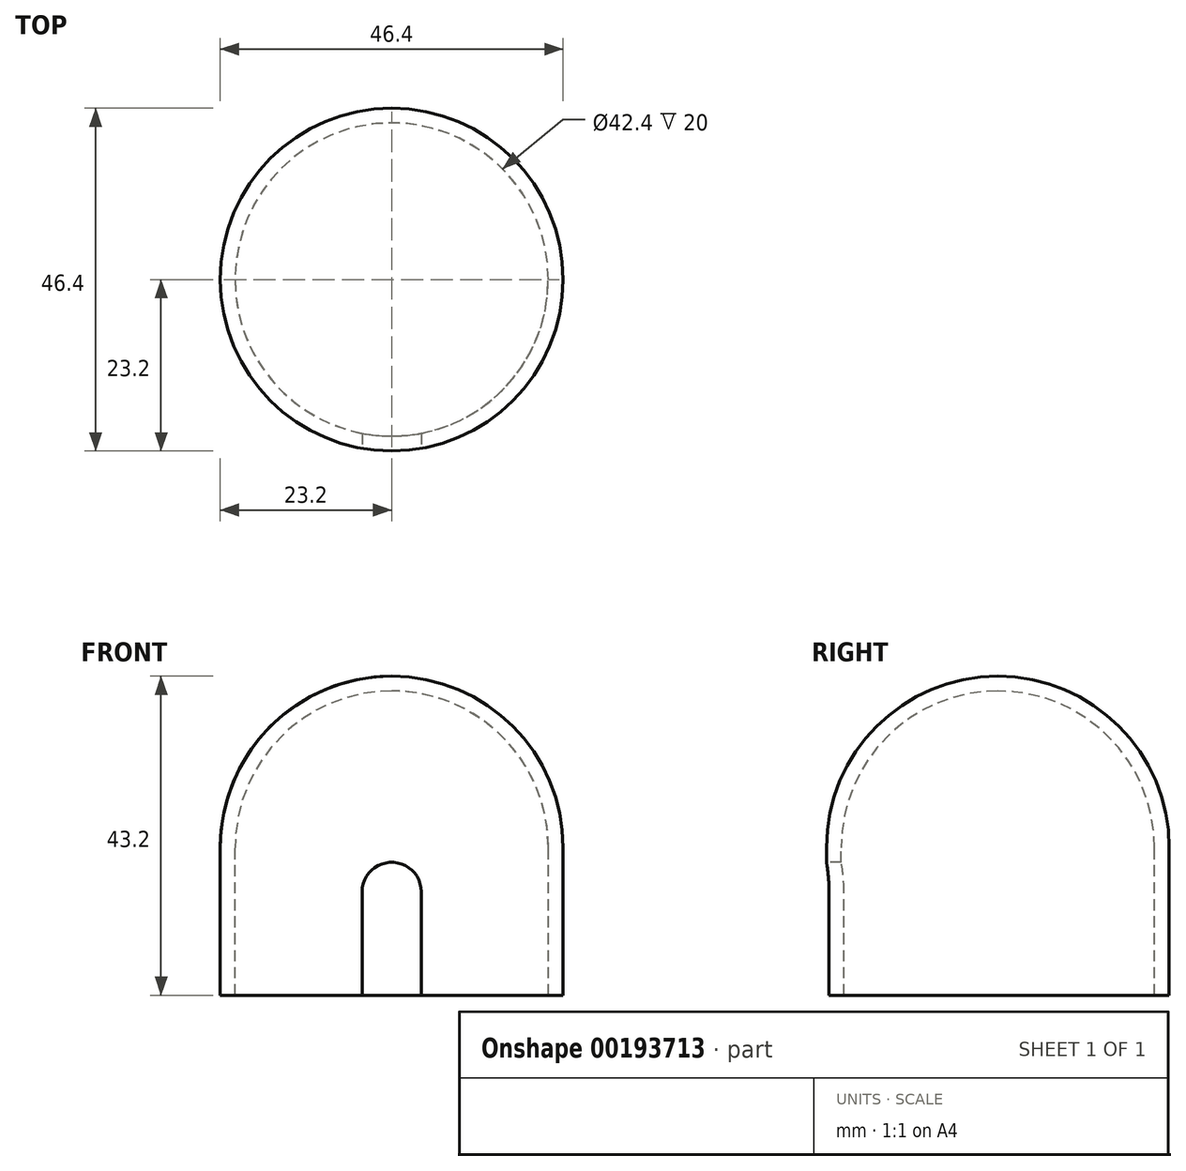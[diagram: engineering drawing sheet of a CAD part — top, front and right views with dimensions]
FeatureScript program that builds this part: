
annotation { "Feature Type Name" : "Feature", "Feature Type Description" : "" }
export const myFeature = defineFeature(function(context is Context, id is Id, definition is map)
    precondition{}
    {
        {
            var Q0;
            Q0=qCreatedBy(makeId("Front.planeOp"),FACE);
            var sketch = newSketch(context, id + "F0", { "sketchPlane" : qUnion([Q0])});
            skLineSegment(sketch, "E0", {"start": v(-21.2, 0) * mm, "end": v(-21.2, 20) * mm});
            skArc(sketch, "E1", {"start": v(-21.2, 20) * mm, "mid": v(-15, 35) * mm, "end": v(0, 41.2) * mm});
            skArc(sketch, "E2.0", {"start": v(-23.2, 20) * mm, "mid": v(-16.4, 36.4) * mm, "end": v(0, 43.2) * mm});
            skLineSegment(sketch, "E2.1", {"start": v(-23.2, 0) * mm, "end": v(-23.2, 20) * mm});
            skLineSegment(sketch, "E3", {"start": v(-23.2, 0) * mm, "end": v(-21.2, 0) * mm});
            skLineSegment(sketch, "E4", {"start": v(0, 41.2) * mm, "end": v(0, 43.2) * mm});
            skSolve(sketch);
        }
        {
            var Q0;
            Q0=qCreatedBy(makeId("Front.planeOp"),FACE);
            var sketch = newSketch(context, id + "F1", { "sketchPlane" : qUnion([Q0])});
            skLineSegment(sketch, "E5", {"start": v(0, 50.12) * mm, "end": v(0, -26.28) * mm, "construction": true});
            skSolve(sketch);
        }
        {
            var Q0;
            Q0 = qSketchRegion(id + "F0", true);
            var Q1;
            Q1=sQuery(id+"F1.wireOp",EDGE,"E5");
            revolve(context, id + "F2", {"entities" : qUnion([Q0]), "axis" : qUnion([Q1]), "revolveType" : RevolveType.FULL});
        }
        {
            var Q0;
            Q0=qCreatedBy(makeId("Front.planeOp"),FACE);
            cPlane(context, id + "F3", {"entities" : qUnion([Q0]), "cplaneType" : CPlaneType.OFFSET, "offset" : 25 * mm, "width" : 150 * mm, "height" : 150 * mm});
        }
        {
            var Q0;
            Q0=qCreatedBy(id+"F3.planeOp",FACE);
            var sketch = newSketch(context, id + "F4", { "sketchPlane" : qUnion([Q0])});
            skArc(sketch, "E6", {"start": v(4, 14) * mm, "mid": v(0, 18) * mm, "end": v(-4, 14) * mm});
            skLineSegment(sketch, "E7", {"start": v(-4, 14) * mm, "end": v(-4, 0) * mm});
            skLineSegment(sketch, "E8", {"start": v(-4, 0) * mm, "end": v(4, 0) * mm});
            skLineSegment(sketch, "E9", {"start": v(4, 0) * mm, "end": v(4, 14) * mm});
            skSolve(sketch);
        }
        {
            var Q0;
            Q0 = qSketchRegion(id + "F4", true);
            extrude(context, id + "F5", {"entities" : qUnion([Q0]), "operationType" : NewBodyOperationType.REMOVE, "oppositeDirection" : true, "depth" : 12 * mm});
        }
    });
